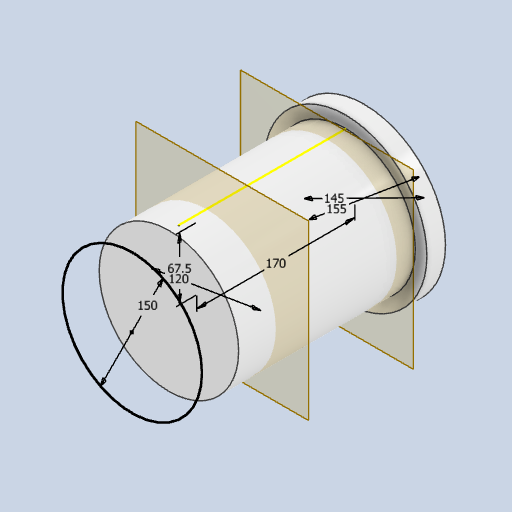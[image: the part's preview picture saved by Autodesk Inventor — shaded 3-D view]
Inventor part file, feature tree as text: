
AUTODESK INVENTOR PART (.ipt)
format: ipt  version: 2024.2 (Build 282272000, 272)  size: 532,992 bytes
history: native  units: in
note: dims shown in document units (in); Inventor stores cm internally (conversion verified against a paired STEP export)
features: thread x15, sketch x11, extrude x10, other x3, plane x3, hole x2
ambient origin geometry x8: Origin, YZ Plane, XZ Plane, XY Plane, X Axis, Y Axis, Z Axis, Center Point
bodies: Solid1 (feature_tree)
feature tree (44):
  other  "{BB8FE430-83BF-418D-8DF9-9B323D3DB9B9}"
  other  "Groove"
  extrude  "Extrusion1"  Depth=5.9055in
  plane  "Work Plane1"
  plane  "Work Plane2"
  extrude  "Extrusion3"  Depth=9.4488in
  plane  "Work Plane3"
  sketch  "Sketch17"  dims[d5=5.9055in d6=6.6929in]
  sketch  "Sketch19"  dims[d7=2.6575in d12=6.2992in]
  extrude  "Extrusion7"  Depth=6.6929in
  extrude  "Extrusion8"  Depth=6.2992in
  extrude  "Extrusion9"  Depth=0.3937in TaperAngle=15.0deg
  thread  "Thread14"  [1 undecoded]
  thread  "Thread15"  [1 undecoded]
  thread  "Thread16"  [1 undecoded]
  thread  "Thread17"  [1 undecoded]
  thread  "Thread18"  [1 undecoded]
  thread  "Thread19"  [1 undecoded]
  sketch  "Sketch47"  dims[d152=5.5118in d153=5.1181in d154=0.1969in d155=1.1811in d157=360.0deg d159=0.1969in d160=0.1969in d161=1.1811in d163=360.0deg d165=0.7874in d166=0.0in d167=0.7874in d168=0.0in d169=0.3937in d170=0.0in]
  extrude  "Extrusion10"  Depth=2.3622in TaperAngle=360.0deg
  hole  "Hole9"  [1 undecoded]
  extrude  "Extrusion12"  Depth=0.3937in
  thread  "Thread3"  [1 undecoded]
  thread  "Thread4"  [1 undecoded]
  thread  "Thread5"  [1 undecoded]
  thread  "Thread6"  [1 undecoded]
  thread  "Thread7"  [1 undecoded]
  thread  "Thread8"  [1 undecoded]
  thread  "Thread9"  [1 undecoded]
  thread  "Thread10"  [1 undecoded]
  sketch  "Sketch52"  dims[d171=6.8898in d172=0.7874in d173=0.0in]
  extrude  "Extrusion13"  Depth=0.7874in TaperAngle=0.0deg
  other  "Groove1"
  extrude  "Extrusion14"  Depth=0.3937in
  hole  "Hole12"  [1 undecoded]
  thread  "Thread13"  [1 undecoded]
  sketch  "Sketch5"  dims[d0=5.5118in d1=5.9055in]
  sketch  "Sketch22"  dims[d13=4.7244in d18=15.0deg d19=4.7244in d21=0.3937in d22=0.0in d23=5.9055in d34=5.5118in d53=-5.1181in d106=2.3622in d108=360.0deg]
  sketch  "Sketch23"  dims[d111=2.3622in d112=360.0deg d113=5.5118in d114=5.9055in d115=4.7244in d116=15.0deg d118=0.0in d119=0.3937in d120=5.1181in]
  sketch  "Sketch24"  dims[d121=0.1969in d122=2.3622in d124=360.0deg]
  sketch  "Sketch25"  dims[d138=5.1181in d141=2.3622in d143=360.0deg]
  sketch  "Sketch54"  dims[d174=6.4961in d175=0.1969in d176=3.1496in d178=360.0deg d182=0.1936in d183=0.4724in d184=0.1575in d185=0.0787in d186=90.0deg d187=0.6732in d188=0.8108in d189=0.1969in d190=0.0in d204=0.3937in d205=0.0in d206=0.3937in d207=0.0in d208=0.3937in d209=0.0in d210=0.3937in d211=0.0in d212=0.3937in d213=0.0in d214=0.3937in d215=0.0in d216=0.3937in d217=0.0in d218=0.3937in d219=0.0in d229=0.0074in d231=60.0deg d250=0.0049in d252=60.0deg d271=0.0049in d273=60.0deg d292=0.0049in d294=60.0deg d313=0.0049in d315=60.0deg d334=0.0049in d336=60.0deg d355=0.0049in d357=60.0deg d376=0.0049in d378=60.0deg d397=0.0049in d399=60.0deg d416=0.3937in d417=0.0in d418=0.1969in d419=0.0in d422=5.7087in d423=6.1024in d424=0.4921in d425=0.0in d426=0.4921in d427=0.0in d439=4.7244in d440=0.4016in d452=0.0086in d454=60.0deg d464=0.4016in d465=0.2362in d466=0.1575in d467=0.0787in d468=90.0deg d469=0.4921in d470=0.8108in d471=0.1969in d472=0.0in d480=0.3779in d491=0.3937in d492=0.0in d493=0.3937in d494=0.0in d495=0.3937in d496=0.0in d497=0.3937in d498=0.0in d499=0.3937in d500=0.0in d501=0.3937in d502=0.0in d96=0.0197in d97=0.0344in d98=0.0197in d99=0.0344in d156=0.0197in d191=0.0025in d192=0.0295in d193=0.0148in d420=0.0197in d421=0.0344in]
  extrude  "Extrusion6"  Depth=0.3937in TaperAngle=0.0deg
  sketch  "Sketch16"  dims[d2=7.4803in d3=0.0in d4=9.4488in]
note: 17 required parameter values undecoded (feature->parameter linkage not recoverable at this tier; creation-order binding heuristic only, values carry confidence <= 0.55)
